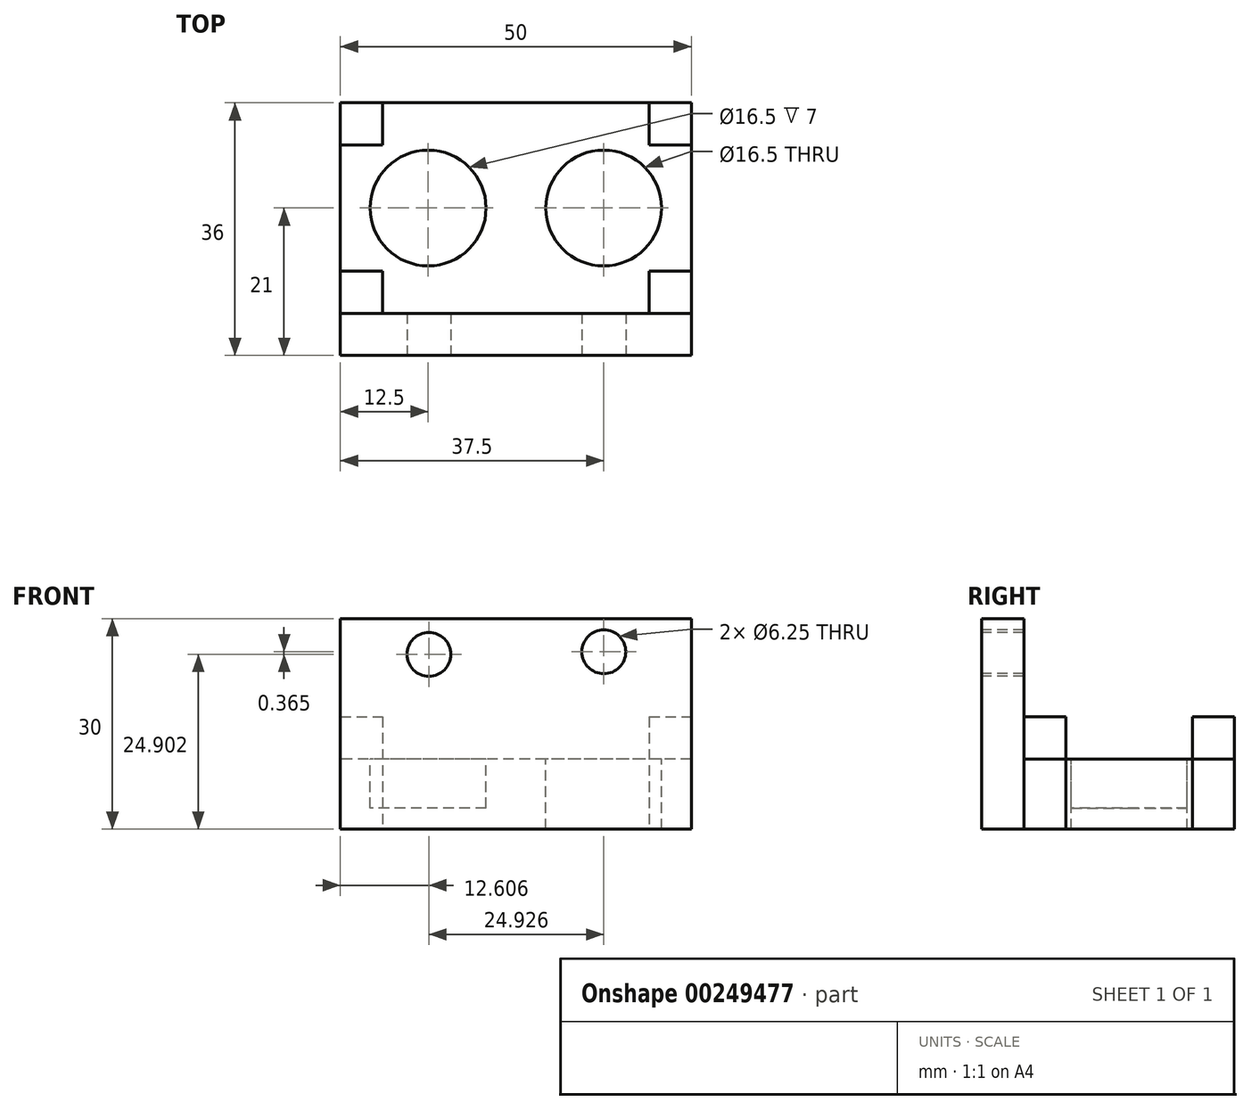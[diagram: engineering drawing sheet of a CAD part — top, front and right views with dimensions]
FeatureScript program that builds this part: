
annotation { "Feature Type Name" : "Feature", "Feature Type Description" : "" }
export const myFeature = defineFeature(function(context is Context, id is Id, definition is map)
    precondition{}
    {
        {
            var Q0;
            Q0=qCreatedBy(makeId("Top.planeOp"),FACE);
            var sketch = newSketch(context, id + "F0", { "sketchPlane" : qUnion([Q0])});
            skLineSegment(sketch, "E0.bottom", {"start": v(25, 15) * mm, "end": v(-25, 15) * mm});
            skLineSegment(sketch, "E0.top", {"start": v(25, -15) * mm, "end": v(-25, -15) * mm});
            skLineSegment(sketch, "E0.left", {"start": v(25, 15) * mm, "end": v(25, -15) * mm});
            skLineSegment(sketch, "E0.right", {"start": v(-25, 15) * mm, "end": v(-25, -15) * mm});
            skPoint(sketch, "E0.middle", {"position": v(0, 0) * mm});
            skSolve(sketch);
        }
        {
            var Q0;
            Q0=qCreatedBy(makeId("Top.planeOp"),FACE);
            var sketch = newSketch(context, id + "F1", { "sketchPlane" : qUnion([Q0])});
            skLineSegment(sketch, "E1.bottom", {"start": v(-25, 15) * mm, "end": v(-19, 15) * mm});
            skLineSegment(sketch, "E1.top", {"start": v(-25, 9) * mm, "end": v(-19, 9) * mm});
            skLineSegment(sketch, "E1.left", {"start": v(-25, 15) * mm, "end": v(-25, 9) * mm});
            skLineSegment(sketch, "E1.right", {"start": v(-19, 15) * mm, "end": v(-19, 9) * mm});
            skSolve(sketch);
        }
        {
            var Q0;
            Q0=qCreatedBy(makeId("Top.planeOp"),FACE);
            var sketch = newSketch(context, id + "F2", { "sketchPlane" : qUnion([Q0])});
            skLineSegment(sketch, "E2.bottom", {"start": v(-25, -9) * mm, "end": v(-19, -9) * mm});
            skLineSegment(sketch, "E2.top", {"start": v(-25, -15) * mm, "end": v(-19, -15) * mm});
            skLineSegment(sketch, "E2.left", {"start": v(-25, -9) * mm, "end": v(-25, -15) * mm});
            skLineSegment(sketch, "E2.right", {"start": v(-19, -9) * mm, "end": v(-19, -15) * mm});
            skLineSegment(sketch, "E3.bottom", {"start": v(19, -9) * mm, "end": v(25, -9) * mm});
            skLineSegment(sketch, "E3.top", {"start": v(19, -15) * mm, "end": v(25, -15) * mm});
            skLineSegment(sketch, "E3.left", {"start": v(19, -9) * mm, "end": v(19, -15) * mm});
            skLineSegment(sketch, "E3.right", {"start": v(25, -9) * mm, "end": v(25, -15) * mm});
            skLineSegment(sketch, "E4.bottom", {"start": v(19, 15) * mm, "end": v(25, 15) * mm});
            skLineSegment(sketch, "E4.top", {"start": v(19, 9) * mm, "end": v(25, 9) * mm});
            skLineSegment(sketch, "E4.left", {"start": v(19, 15) * mm, "end": v(19, 9) * mm});
            skLineSegment(sketch, "E4.right", {"start": v(25, 15) * mm, "end": v(25, 9) * mm});
            skSolve(sketch);
        }
        {
            var Q0;
            Q0=qCreatedBy(makeId("Top.planeOp"),FACE);
            var sketch = newSketch(context, id + "F3", { "sketchPlane" : qUnion([Q0])});
            skLineSegment(sketch, "E5", {"start": v(0, 15) * mm, "end": v(0, -15) * mm, "construction": true});
            skSolve(sketch);
        }
        {
            var Q0;
            Q0=qCreatedBy(makeId("Top.planeOp"),FACE);
            var sketch = newSketch(context, id + "F4", { "sketchPlane" : qUnion([Q0])});
            skLineSegment(sketch, "E6", {"start": v(-12.5, 14.52) * mm, "end": v(-12.5, -14.36) * mm, "construction": true});
            skSolve(sketch);
        }
        {
            var Q0;
            Q0=qCreatedBy(makeId("Top.planeOp"),FACE);
            var sketch = newSketch(context, id + "F5", { "sketchPlane" : qUnion([Q0])});
            skLineSegment(sketch, "E7", {"start": v(12.5, 19.39) * mm, "end": v(12.5, -19.66) * mm, "construction": true});
            skSolve(sketch);
        }
        {
            var Q0;
            Q0=qCreatedBy(makeId("Top.planeOp"),FACE);
            var sketch = newSketch(context, id + "F6", { "sketchPlane" : qUnion([Q0])});
            skLineSegment(sketch, "E8.bottom", {"start": v(-25, -15) * mm, "end": v(25, -15) * mm});
            skLineSegment(sketch, "E8.top", {"start": v(-25, -21) * mm, "end": v(25, -21) * mm});
            skLineSegment(sketch, "E8.left", {"start": v(-25, -15) * mm, "end": v(-25, -21) * mm});
            skLineSegment(sketch, "E8.right", {"start": v(25, -15) * mm, "end": v(25, -21) * mm});
            skSolve(sketch);
        }
        {
            var Q0;
            Q0=makeQuery(id+"F6.imprint","IMPRINT",FACE,{"disambiguationData":[TD([[makeQuery(id+"F6.imprint","IMPRINT",EDGE,{"derivedFrom":sQuery(id+"F6.wireOp",EDGE,"E8.bottom")}),-1.0]])]});
            extrude(context, id + "F7", {"entities" : qUnion([Q0]), "depth" : 30 * mm});
        }
        {
            var Q0;
            Q0=makeQuery(id+"F0.imprint","IMPRINT",FACE,{"disambiguationData":[TD([[makeQuery(id+"F0.imprint","IMPRINT",EDGE,{"derivedFrom":sQuery(id+"F0.wireOp",EDGE,"E0.bottom")}),1.0]])]});
            extrude(context, id + "F8", {"entities" : qUnion([Q0]), "depth" : 10 * mm});
        }
        {
            var Q0;
            Q0=makeQuery(id+"F8.opExtrude","CAP_FACE",FACE,{"disambiguationData":[OSD([sQuery(id+"F0.wireOp",EDGE,"E0.bottom"),sQuery(id+"F0.wireOp",EDGE,"E0.top"),sQuery(id+"F0.wireOp",EDGE,"E0.left"),sQuery(id+"F0.wireOp",EDGE,"E0.right")])],"isStart":false});
            var sketch = newSketch(context, id + "F9", { "sketchPlane" : qUnion([Q0])});
            skCircle(sketch, "E9", {"center": v(-12.5, 0) * mm, "radius": 8.25 * mm});
            skSolve(sketch);
        }
        {
            var Q0;
            Q0=makeQuery(id+"F8.opExtrude","CAP_FACE",FACE,{"disambiguationData":[OSD([sQuery(id+"F0.wireOp",EDGE,"E0.bottom"),sQuery(id+"F0.wireOp",EDGE,"E0.top"),sQuery(id+"F0.wireOp",EDGE,"E0.left"),sQuery(id+"F0.wireOp",EDGE,"E0.right")])],"isStart":false});
            var sketch = newSketch(context, id + "F10", { "sketchPlane" : qUnion([Q0])});
            skCircle(sketch, "E10", {"center": v(12.5, 0) * mm, "radius": 8.25 * mm});
            skSolve(sketch);
        }
        {
            var Q0;
            Q0=makeQuery(id+"F1.imprint","IMPRINT",FACE,{"disambiguationData":[TD([[makeQuery(id+"F1.imprint","IMPRINT",EDGE,{"derivedFrom":sQuery(id+"F1.wireOp",EDGE,"E1.bottom")}),-1.0]])]});
            var Q1;
            Q1=makeQuery(id+"F2.imprint","IMPRINT",FACE,{"disambiguationData":[TD([[makeQuery(id+"F2.imprint","IMPRINT",EDGE,{"derivedFrom":sQuery(id+"F2.wireOp",EDGE,"E4.bottom")}),-1.0]])]});
            var Q2;
            Q2=makeQuery(id+"F2.imprint","IMPRINT",FACE,{"disambiguationData":[TD([[makeQuery(id+"F2.imprint","IMPRINT",EDGE,{"derivedFrom":sQuery(id+"F2.wireOp",EDGE,"E3.bottom")}),-1.0]])]});
            var Q3;
            Q3=makeQuery(id+"F2.imprint","IMPRINT",FACE,{"disambiguationData":[TD([[makeQuery(id+"F2.imprint","IMPRINT",EDGE,{"derivedFrom":sQuery(id+"F2.wireOp",EDGE,"E2.bottom")}),-1.0]])]});
            extrude(context, id + "F11", {"entities" : qUnion([Q0, Q1, Q2, Q3]), "depth" : 16 * mm});
        }
        {
            var Q0;
            Q0=makeQuery(id+"F7.opExtrude","SWEPT_FACE",FACE,{"disambiguationData":[OSD([sQuery(id+"F6.wireOp",EDGE,"E8.top")])]});
            var sketch = newSketch(context, id + "F12", { "sketchPlane" : qUnion([Q0])});
            skLineSegment(sketch, "E11", {"start": v(-25, 25) * mm, "end": v(25, 25) * mm, "construction": true});
            skSolve(sketch);
        }
        {
            var Q0;
            {var subQ0=sQuery(id+"F6.wireOp",EDGE,"E8.top");Q0=makeQuery(id+"F12.imprint","IMPRINT",FACE,{"disambiguationData":[TD([[makeQuery(id+"F12.imprint","IMPRINT",EDGE,{"derivedFrom":makeQuery(id+"F7.opExtrude","CAP_EDGE",EDGE,{"disambiguationData":[OSD([subQ0])],"isStart":true})}),1.0]])]});}
            var sketch = newSketch(context, id + "F13", { "sketchPlane" : qUnion([Q0])});
            skCircle(sketch, "E12", {"center": v(-12.4, 24.9) * mm, "radius": 3.12 * mm});
            skCircle(sketch, "E13", {"center": v(12.53, 25.27) * mm, "radius": 3.12 * mm});
            skSolve(sketch);
        }
        {
            var Q0;
            Q0=makeQuery(id+"F13.imprint","IMPRINT",FACE,{"disambiguationData":[TD([[makeQuery(id+"F13.imprint","IMPRINT",EDGE,{"derivedFrom":sQuery(id+"F13.wireOp",EDGE,"E12")}),1.0]])]});
            var Q1;
            Q1=makeQuery(id+"F13.imprint","IMPRINT",FACE,{"disambiguationData":[TD([[makeQuery(id+"F13.imprint","IMPRINT",EDGE,{"derivedFrom":sQuery(id+"F13.wireOp",EDGE,"E13")}),1.0]])]});
            var Q2;
            Q2=sQuery(id+"F13.wireOp",EDGE,"E12");
            var Q3;
            Q3=sQuery(id+"F13.wireOp",EDGE,"E13");
            extrude(context, id + "F14", {"entities" : qUnion([Q0, Q1]), "operationType" : NewBodyOperationType.REMOVE, "surfaceEntities" : qUnion([Q2, Q3]), "oppositeDirection" : true, "depth" : 10 * mm});
        }
        {
            var Q0;
            Q0=makeQuery(id+"F9.imprint","IMPRINT",FACE,{"disambiguationData":[TD([[makeQuery(id+"F9.imprint","IMPRINT",EDGE,{"derivedFrom":sQuery(id+"F9.wireOp",EDGE,"E9")}),1.0]])]});
            var Q1;
            Q1=sQuery(id+"F9.wireOp",EDGE,"E9");
            extrude(context, id + "F15", {"entities" : qUnion([Q0]), "operationType" : NewBodyOperationType.REMOVE, "surfaceEntities" : qUnion([Q1]), "oppositeDirection" : true, "depth" : 7 * mm});
        }
        {
            var Q0;
            Q0=makeQuery(id+"F10.imprint","IMPRINT",FACE,{"disambiguationData":[TD([[makeQuery(id+"F10.imprint","IMPRINT",EDGE,{"derivedFrom":sQuery(id+"F10.wireOp",EDGE,"E10")}),1.0]])]});
            var Q1;
            Q1=sQuery(id+"F10.wireOp",EDGE,"E10");
            extrude(context, id + "F16", {"entities" : qUnion([Q0]), "operationType" : NewBodyOperationType.REMOVE, "surfaceEntities" : qUnion([Q1]), "oppositeDirection" : true, "depth" : 10 * mm});
        }
    });
